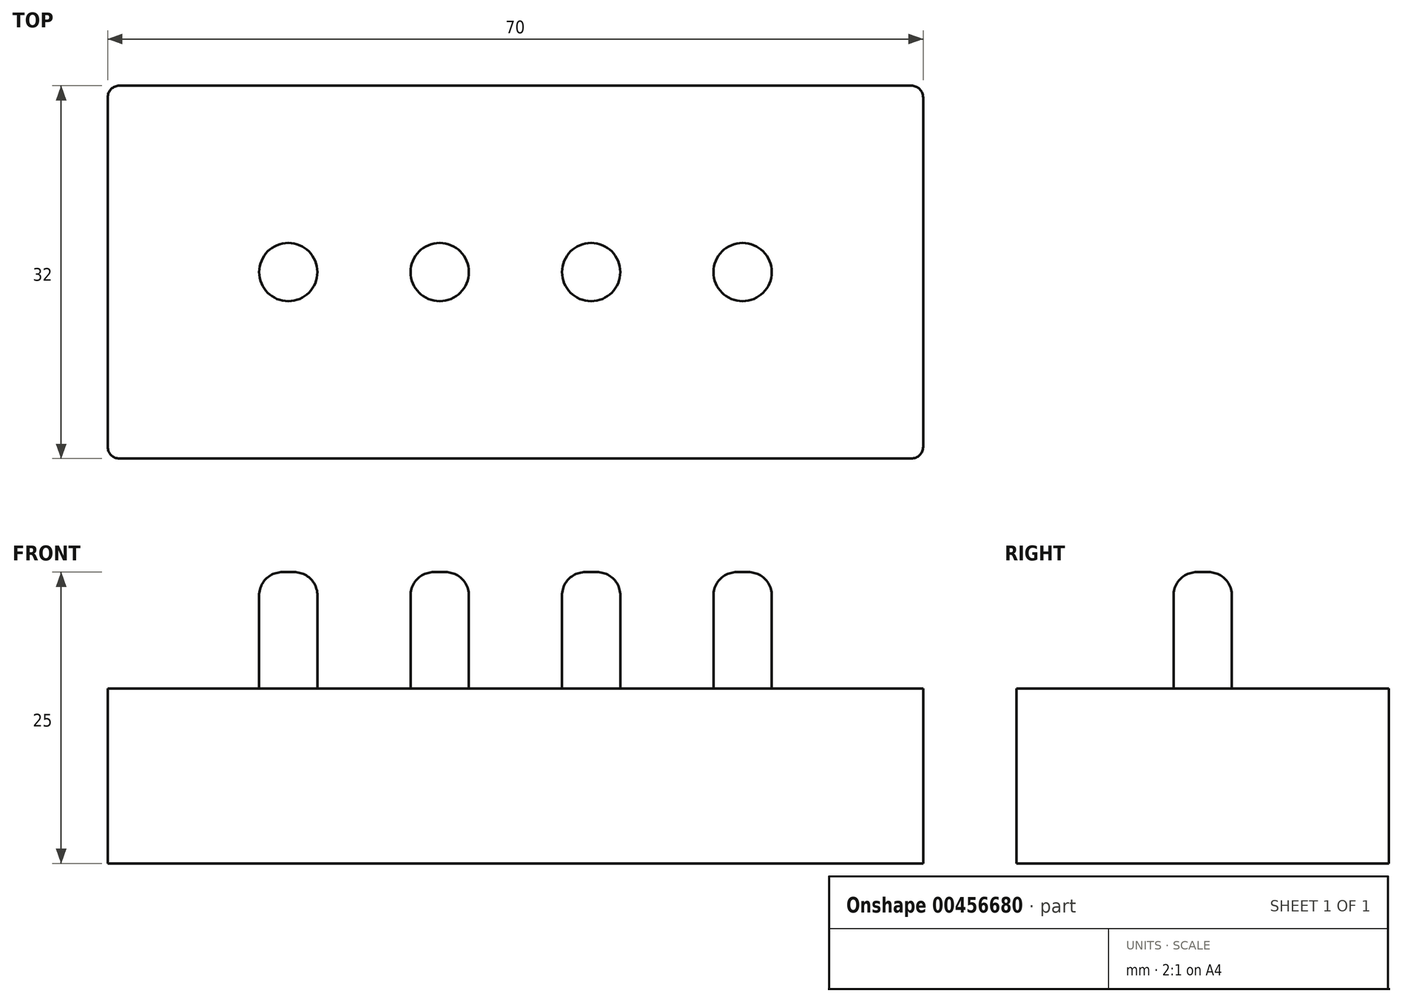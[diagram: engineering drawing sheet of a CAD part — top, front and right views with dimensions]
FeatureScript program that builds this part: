
annotation { "Feature Type Name" : "Feature", "Feature Type Description" : "" }
export const myFeature = defineFeature(function(context is Context, id is Id, definition is map)
    precondition{}
    {
        {
            var Q0;
            Q0=qCreatedBy(makeId("Top.planeOp"),FACE);
            var sketch = newSketch(context, id + "F0", { "sketchPlane" : qUnion([Q0])});
            skLineSegment(sketch, "E0.bottom", {"start": v(-34, 16) * mm, "end": v(34, 16) * mm});
            skLineSegment(sketch, "E0.top", {"start": v(-34, -16) * mm, "end": v(34, -16) * mm});
            skLineSegment(sketch, "E0.left", {"start": v(-35, 15) * mm, "end": v(-35, -15) * mm});
            skLineSegment(sketch, "E0.right", {"start": v(35, 15) * mm, "end": v(35, -15) * mm});
            skPoint(sketch, "E0.middle", {"position": v(0, 0) * mm});
            skLineSegment(sketch, "E1", {"start": v(-19.5, 22.14) * mm, "end": v(-19.5, -27.46) * mm, "construction": true});
            skLineSegment(sketch, "E2", {"start": v(-6.5, 21.65) * mm, "end": v(-6.5, -27.22) * mm, "construction": true});
            skLineSegment(sketch, "E3", {"start": v(6.5, 21.17) * mm, "end": v(6.5, -28.91) * mm, "construction": true});
            skLineSegment(sketch, "E4", {"start": v(19.5, 21.41) * mm, "end": v(19.5, -26) * mm, "construction": true});
            skLineSegment(sketch, "E5", {"start": v(-46.7, 0) * mm, "end": v(45.48, 0) * mm, "construction": true});
            skPoint(sketch, "E5.endSnap0", {"position": v(35, 0) * mm});
            skPoint(sketch, "E6.visualSharp", {"position": v(-35, 16) * mm});
            skArc(sketch, "E6.filletArc", {"start": v(-34, 16) * mm, "mid": v(-34.7, 15.7) * mm, "end": v(-35, 15) * mm});
            skPoint(sketch, "E7.visualSharp", {"position": v(35, 16) * mm});
            skArc(sketch, "E7.filletArc", {"start": v(35, 15) * mm, "mid": v(34.7, 15.7) * mm, "end": v(34, 16) * mm});
            skPoint(sketch, "E8.visualSharp", {"position": v(35, -16) * mm});
            skArc(sketch, "E8.filletArc", {"start": v(34, -16) * mm, "mid": v(34.7, -15.7) * mm, "end": v(35, -15) * mm});
            skPoint(sketch, "E9.visualSharp", {"position": v(-35, -16) * mm});
            skArc(sketch, "E9.filletArc", {"start": v(-35, -15) * mm, "mid": v(-34.7, -15.7) * mm, "end": v(-34, -16) * mm});
            skSolve(sketch);
        }
        {
            var Q0;
            Q0 = qSketchRegion(id + "F0", true);
            var Q1;
            Q1=makeQuery(id+"F0.imprint","IMPRINT",FACE,{"disambiguationData":[TD([[makeQuery(id+"F0.imprint","IMPRINT",EDGE,{"derivedFrom":sQuery(id+"F0.wireOp",EDGE,"E0.bottom")}),-1.0]])]});
            extrude(context, id + "F1", {"entities" : qUnion([Q0, Q1]), "oppositeDirection" : true, "depth" : 15 * mm});
        }
        {
            var Q0;
            Q0=makeQuery(id+"F1.opExtrude","CAP_FACE",FACE,{"disambiguationData":[OSD([sQuery(id+"F0.wireOp",EDGE,"E0.bottom"),sQuery(id+"F0.wireOp",EDGE,"E0.top"),sQuery(id+"F0.wireOp",EDGE,"E0.left"),sQuery(id+"F0.wireOp",EDGE,"E0.right")])],"isStart":true});
            var sketch = newSketch(context, id + "F2", { "sketchPlane" : qUnion([Q0])});
            skLineSegment(sketch, "E10", {"start": v(-19.5, 55.67) * mm, "end": v(-19.5, -53.46) * mm, "construction": true});
            skLineSegment(sketch, "E11", {"start": v(-6.5, 52.55) * mm, "end": v(-6.5, -59.39) * mm, "construction": true});
            skLineSegment(sketch, "E12", {"start": v(6.5, 56.6) * mm, "end": v(6.5, -55.33) * mm, "construction": true});
            skLineSegment(sketch, "E13", {"start": v(19.5, 51.48) * mm, "end": v(19.5, -49.22) * mm, "construction": true});
            skLineSegment(sketch, "E14", {"start": v(-59.64, 0) * mm, "end": v(55.45, 0) * mm, "construction": true});
            skCircle(sketch, "E15", {"center": v(-19.5, 0) * mm, "radius": 2.5 * mm});
            skCircle(sketch, "E16", {"center": v(-6.5, 0) * mm, "radius": 2.5 * mm});
            skCircle(sketch, "E17", {"center": v(6.5, 0) * mm, "radius": 2.5 * mm});
            skCircle(sketch, "E18", {"center": v(19.5, 0) * mm, "radius": 2.5 * mm});
            skSolve(sketch);
        }
        {
            var Q0;
            Q0=makeQuery(id+"F2.imprint","IMPRINT",FACE,{"disambiguationData":[TD([[makeQuery(id+"F2.imprint","IMPRINT",EDGE,{"derivedFrom":sQuery(id+"F2.wireOp",EDGE,"E15")}),1.0]])]});
            var Q1;
            Q1=makeQuery(id+"F2.imprint","IMPRINT",FACE,{"disambiguationData":[TD([[makeQuery(id+"F2.imprint","IMPRINT",EDGE,{"derivedFrom":sQuery(id+"F2.wireOp",EDGE,"E16")}),1.0]])]});
            var Q2;
            Q2=makeQuery(id+"F2.imprint","IMPRINT",FACE,{"disambiguationData":[TD([[makeQuery(id+"F2.imprint","IMPRINT",EDGE,{"derivedFrom":sQuery(id+"F2.wireOp",EDGE,"E17")}),1.0]])]});
            var Q3;
            Q3=makeQuery(id+"F2.imprint","IMPRINT",FACE,{"disambiguationData":[TD([[makeQuery(id+"F2.imprint","IMPRINT",EDGE,{"derivedFrom":sQuery(id+"F2.wireOp",EDGE,"E18")}),1.0]])]});
            extrude(context, id + "F3", {"entities" : qUnion([Q0, Q1, Q2, Q3]), "operationType" : NewBodyOperationType.ADD, "depth" : 10 * mm});
        }
        {
            var Q0;
            Q0=makeQuery(id+"F3.opExtrude","CAP_EDGE",EDGE,{"disambiguationData":[OSD([sQuery(id+"F2.wireOp",EDGE,"E18")])],"isStart":false});
            var Q1;
            Q1=makeQuery(id+"F3.opExtrude","CAP_EDGE",EDGE,{"disambiguationData":[OSD([sQuery(id+"F2.wireOp",EDGE,"E17")])],"isStart":false});
            var Q2;
            Q2=makeQuery(id+"F3.opExtrude","CAP_EDGE",EDGE,{"disambiguationData":[OSD([sQuery(id+"F2.wireOp",EDGE,"E16")])],"isStart":false});
            var Q3;
            Q3=makeQuery(id+"F3.opExtrude","CAP_EDGE",EDGE,{"disambiguationData":[OSD([sQuery(id+"F2.wireOp",EDGE,"E15")])],"isStart":false});
            fillet(context, id + "F4", {"entities" : qUnion([Q0, Q1, Q2, Q3]), "radius" : 2 * mm, "tangentPropagation" : true, "allowEdgeOverflow" : false});
        }
    });
